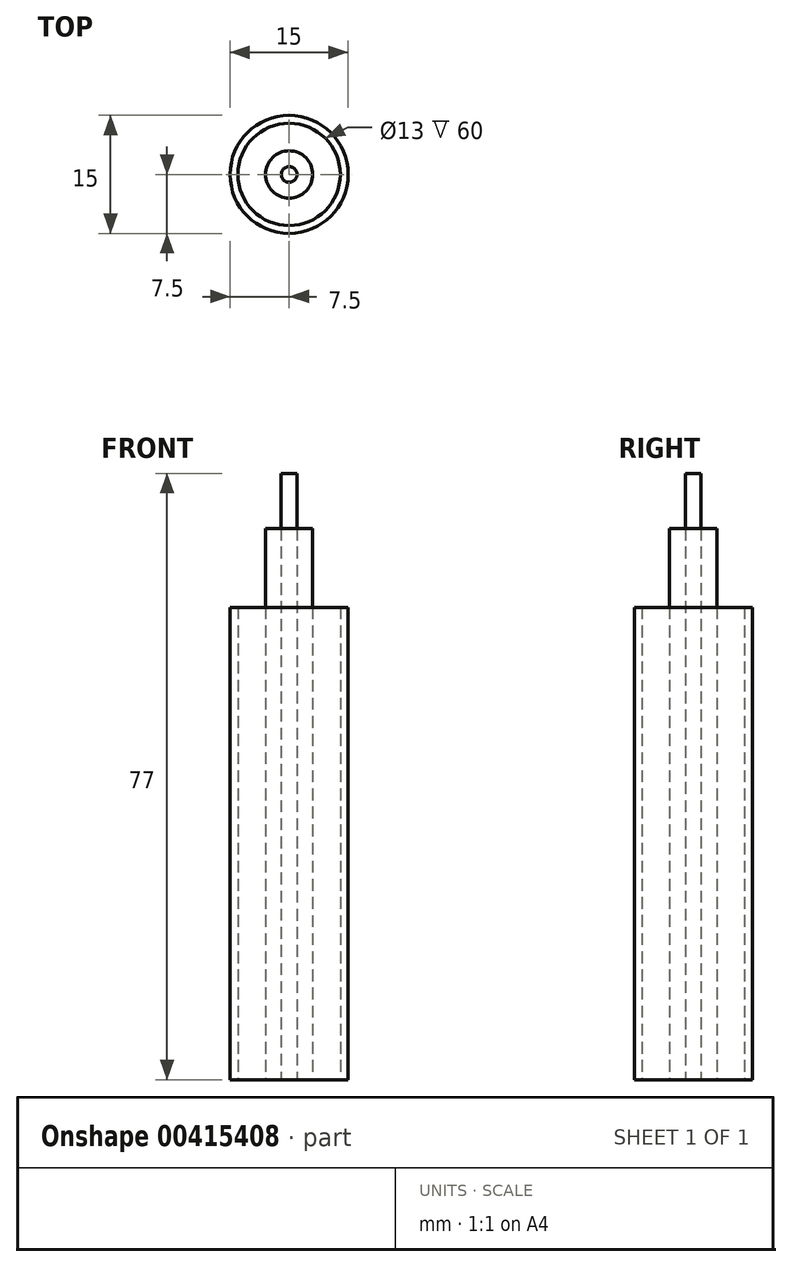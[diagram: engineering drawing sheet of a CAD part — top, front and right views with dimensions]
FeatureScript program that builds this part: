
annotation { "Feature Type Name" : "Feature", "Feature Type Description" : "" }
export const myFeature = defineFeature(function(context is Context, id is Id, definition is map)
    precondition{}
    {
        {
            var Q0;
            Q0=qCreatedBy(makeId("Top.planeOp"),FACE);
            var sketch = newSketch(context, id + "F0", { "sketchPlane" : qUnion([Q0])});
            skCircle(sketch, "E0", {"center": v(0, 0) * mm, "radius": 6.5 * mm});
            skCircle(sketch, "E1", {"center": v(0, 0) * mm, "radius": 7.5 * mm});
            skCircle(sketch, "E2", {"center": v(0, 0) * mm, "radius": 1 * mm});
            skSolve(sketch);
        }
        {
            var Q0;
            Q0=makeQuery(id+"F0.imprint","IMPRINT",FACE,{"disambiguationData":[TD([[makeQuery(id+"F0.imprint","IMPRINT",EDGE,{"derivedFrom":sQuery(id+"F0.wireOp",EDGE,"E0")}),-1.0]])]});
            extrude(context, id + "F1", {"entities" : qUnion([Q0]), "depth" : 60 * mm, "offsetDistance" : 25 * mm});
        }
        {
            var Q0;
            Q0=makeQuery(id+"F0.imprint","IMPRINT",FACE,{"disambiguationData":[TD([[makeQuery(id+"F0.imprint","IMPRINT",EDGE,{"derivedFrom":sQuery(id+"F0.wireOp",EDGE,"E2")}),1.0]])]});
            extrude(context, id + "F2", {"entities" : qUnion([Q0]), "depth" : 77 * mm, "offsetDistance" : 25 * mm});
        }
        {
            var Q0;
            Q0=qCreatedBy(makeId("Top.planeOp"),FACE);
            var sketch = newSketch(context, id + "F3", { "sketchPlane" : qUnion([Q0])});
            skCircle(sketch, "E3", {"center": v(0, 0) * mm, "radius": 3 * mm});
            skSolve(sketch);
        }
        {
            var Q0;
            Q0=makeQuery(id+"F3.imprint","IMPRINT",FACE,{"disambiguationData":[TD([[makeQuery(id+"F3.imprint","IMPRINT",EDGE,{"derivedFrom":sQuery(id+"F3.wireOp",EDGE,"E3")}),1.0]])]});
            extrude(context, id + "F4", {"entities" : qUnion([Q0]), "depth" : 70 * mm, "offsetDistance" : 25 * mm});
        }
    });
